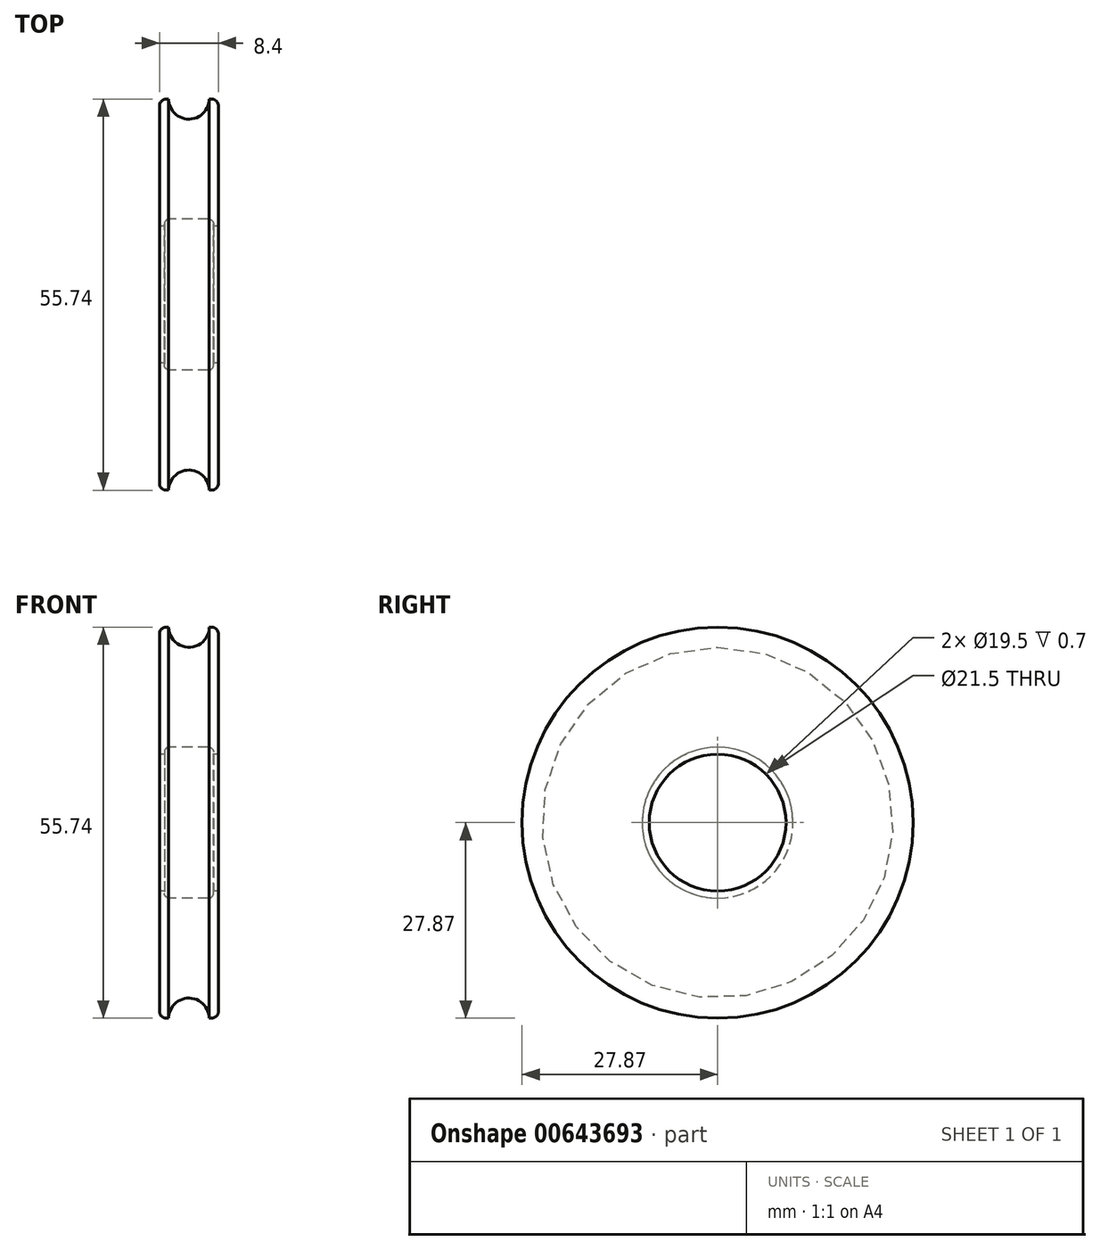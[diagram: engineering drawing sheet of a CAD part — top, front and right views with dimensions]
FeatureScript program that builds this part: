
annotation { "Feature Type Name" : "Feature", "Feature Type Description" : "" }
export const myFeature = defineFeature(function(context is Context, id is Id, definition is map)
    precondition{}
    {
        {
            var Q0;
            Q0=qCreatedBy(makeId("Front.planeOp"),FACE);
            var sketch = newSketch(context, id + "F0", { "sketchPlane" : qUnion([Q0])});
            skLineSegment(sketch, "E0", {"start": v(-37.18, 0) * mm, "end": v(33.4, 0) * mm, "construction": true});
            skLineSegment(sketch, "E1", {"start": v(-9.67, 27.87) * mm, "end": v(-9.67, 9.75) * mm});
            skLineSegment(sketch, "E2", {"start": v(-9.67, 9.75) * mm, "end": v(-8.97, 9.75) * mm});
            skLineSegment(sketch, "E3", {"start": v(-8.97, 9.75) * mm, "end": v(-8.97, 10.75) * mm});
            skLineSegment(sketch, "E4", {"start": v(-8.97, 10.75) * mm, "end": v(-1.97, 10.75) * mm});
            skLineSegment(sketch, "E5", {"start": v(-1.97, 10.75) * mm, "end": v(-1.97, 9.75) * mm});
            skLineSegment(sketch, "E6", {"start": v(-1.97, 9.75) * mm, "end": v(-1.27, 9.75) * mm});
            skLineSegment(sketch, "E7", {"start": v(-1.27, 27.87) * mm, "end": v(-1.27, 9.75) * mm});
            skPoint(sketch, "E8", {"position": v(-8.37, 27.87) * mm});
            skPoint(sketch, "E9", {"position": v(-2.57, 27.87) * mm});
            skArc(sketch, "E10", {"start": v(-8.37, 27.87) * mm, "mid": v(-5.47, 25) * mm, "end": v(-2.57, 27.87) * mm});
            skLineSegment(sketch, "E11", {"start": v(-9.67, 27.87) * mm, "end": v(-8.37, 27.87) * mm});
            skLineSegment(sketch, "E12", {"start": v(-2.57, 27.87) * mm, "end": v(-1.27, 27.87) * mm});
            skLineSegment(sketch, "E13", {"start": v(-5.47, 25) * mm, "end": v(-9.67, 25) * mm, "construction": true});
            skSolve(sketch);
        }
        {
            var Q0;
            Q0=qSketchRegion(id+"F0",true);
            var Q1;
            Q1=sQuery(id+"F0.wireOp",EDGE,"E0");
            revolve(context, id + "F1", {"entities" : qUnion([Q0]), "axis" : qUnion([Q1]), "revolveType" : RevolveType.FULL});
        }
        {
            var Q0;
            Q0=makeQuery(id+"F1.opRevolve","SWEPT_EDGE",EDGE,{"disambiguationData":[OSD([sQuery(id+"F0.wireOp",EDGE,"E3"),sQuery(id+"F0.wireOp",EDGE,"E4")])]});
            var Q1;
            Q1=makeQuery(id+"F1.opRevolve","SWEPT_EDGE",EDGE,{"disambiguationData":[OSD([sQuery(id+"F0.wireOp",EDGE,"E4"),sQuery(id+"F0.wireOp",EDGE,"E5")])]});
            fillet(context, id + "F2", {"entities" : qUnion([Q0, Q1]), "radius" : .7 * mm, "tangentPropagation" : true, "allowEdgeOverflow" : false});
        }
        {
            var Q0;
            Q0=makeQuery(id+"F1.opRevolve","SWEPT_EDGE",EDGE,{"disambiguationData":[OSD([sQuery(id+"F0.wireOp",EDGE,"E1"),sQuery(id+"F0.wireOp",EDGE,"E11")])]});
            var Q1;
            Q1=makeQuery(id+"F1.opRevolve","SWEPT_EDGE",EDGE,{"disambiguationData":[OSD([sQuery(id+"F0.wireOp",EDGE,"E7"),sQuery(id+"F0.wireOp",EDGE,"E12")])]});
            fillet(context, id + "F3", {"entities" : qUnion([Q0, Q1]), "radius" : 1 * mm, "tangentPropagation" : true, "allowEdgeOverflow" : false});
        }
        {
            var Q0;
            Q0=qCreatedBy(makeId("Right.planeOp"),FACE);
            cPlane(context, id + "F4", {"entities" : qUnion([Q0]), "cplaneType" : CPlaneType.OFFSET, "offset" : 5.47 * mm, "oppositeDirection" : true, "width" : 150 * mm, "height" : 150 * mm});
        }
    });
